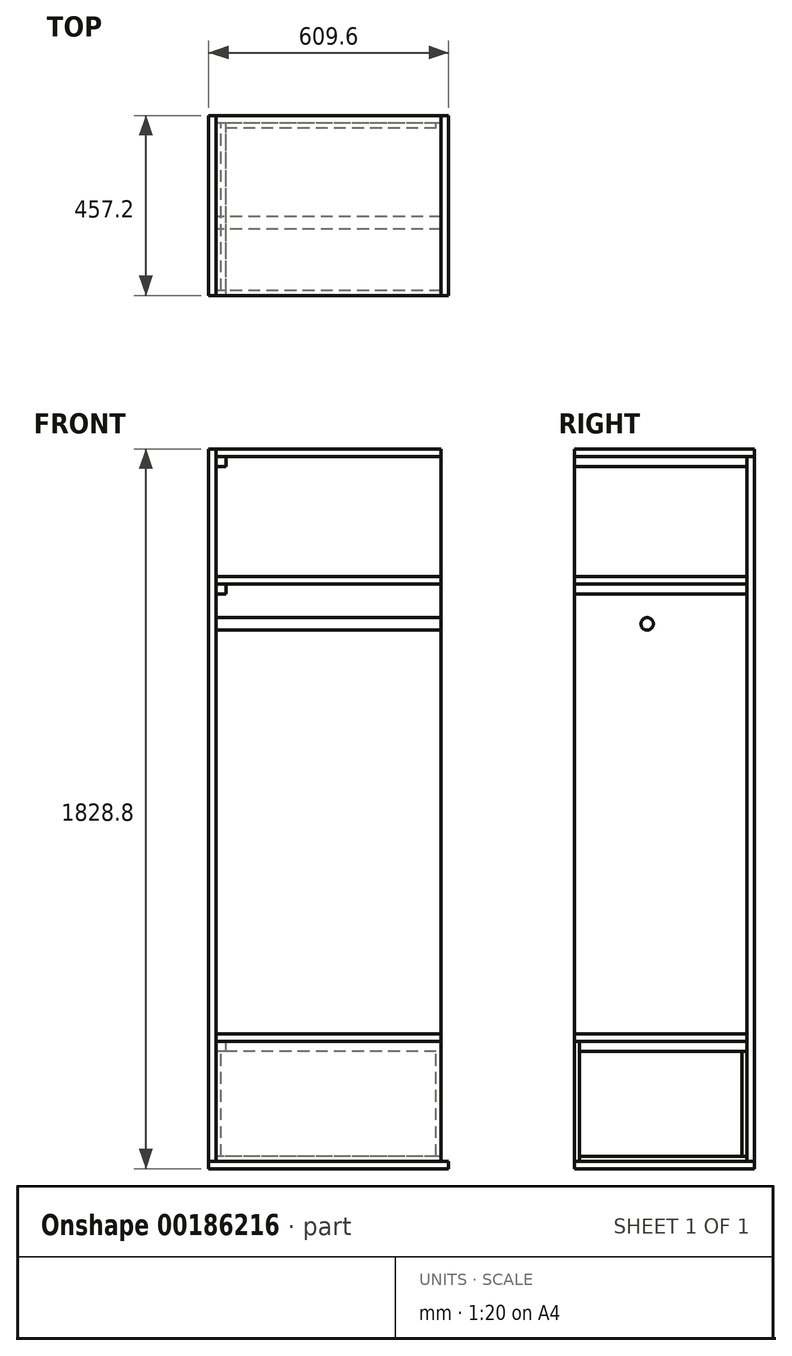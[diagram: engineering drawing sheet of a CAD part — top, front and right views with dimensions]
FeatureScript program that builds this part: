
annotation { "Feature Type Name" : "Feature", "Feature Type Description" : "" }
export const myFeature = defineFeature(function(context is Context, id is Id, definition is map)
    precondition{}
    {
        {
            var Q0;
            Q0=qCreatedBy(makeId("Right.planeOp"),FACE);
            var sketch = newSketch(context, id + "F0", { "sketchPlane" : qUnion([Q0])});
            skLineSegment(sketch, "E0.bottom", {"start": v(-228.6, 914.4) * mm, "end": v(228.6, 914.4) * mm});
            skLineSegment(sketch, "E0.top", {"start": v(-228.6, -914.4) * mm, "end": v(228.6, -914.4) * mm});
            skLineSegment(sketch, "E0.left", {"start": v(-228.6, 914.4) * mm, "end": v(-228.6, -914.4) * mm});
            skLineSegment(sketch, "E0.right", {"start": v(228.6, 914.4) * mm, "end": v(228.6, -914.4) * mm});
            skPoint(sketch, "E0.middle", {"position": v(0, 0) * mm});
            skLineSegment(sketch, "E1", {"start": v(-228.6, 895.35) * mm, "end": v(228.6, 895.35) * mm});
            skLineSegment(sketch, "E2", {"start": v(-228.6, -895.35) * mm, "end": v(228.6, -895.35) * mm});
            skLineSegment(sketch, "E3", {"start": v(-228.6, -571.5) * mm, "end": v(228.6, -571.5) * mm});
            skLineSegment(sketch, "E4", {"start": v(-228.6, -590.55) * mm, "end": v(228.6, -590.55) * mm});
            skLineSegment(sketch, "E5", {"start": v(-228.6, 590.55) * mm, "end": v(228.6, 590.55) * mm});
            skLineSegment(sketch, "E6", {"start": v(-228.6, 571.5) * mm, "end": v(228.6, 571.5) * mm});
            skLineSegment(sketch, "E7", {"start": v(209.55, -914.4) * mm, "end": v(209.55, 914.4) * mm});
            skPoint(sketch, "E8", {"position": v(-44.45, 469.9) * mm});
            skCircle(sketch, "E9", {"center": v(-44.45, 469.9) * mm, "radius": 15.88 * mm});
            skLineSegment(sketch, "E10", {"start": v(-215.9, 914.4) * mm, "end": v(-215.9, -914.4) * mm});
            skLineSegment(sketch, "E11", {"start": v(-228.6, -615.95) * mm, "end": v(209.55, -615.95) * mm});
            skLineSegment(sketch, "E12", {"start": v(209.55, 546.1) * mm, "end": v(-228.6, 546.1) * mm});
            skLineSegment(sketch, "E13", {"start": v(209.55, 869.95) * mm, "end": v(-228.6, 869.95) * mm});
            skLineSegment(sketch, "E14", {"start": v(-215.9, -882.65) * mm, "end": v(209.55, -882.65) * mm});
            skLineSegment(sketch, "E15", {"start": v(196.85, -615.95) * mm, "end": v(196.85, -882.65) * mm});
            skSolve(sketch);
        }
        {
            var Q0;
            {var subQ0=sQuery(id+"F0.wireOp",EDGE,"E0.left");var subQ1=sQuery(id+"F0.wireOp",EDGE,"E0.bottom");var subQ2=makeQuery(id+"F0.imprint","INTERSECT",VERTEX,{"derivedFrom":[subQ1,subQ0]});Q0=makeQuery(id+"F0.imprint","IMPRINT",FACE,{"disambiguationData":[TD([[makeQuery(id+"F0.imprint","IMPRINT",EDGE,{"disambiguationData":[TD([[subQ2,-1.0]])],"derivedFrom":subQ1}),-1.0]])]});}
            var Q1;
            {var subQ0=sQuery(id+"F0.wireOp",EDGE,"E0.right");var subQ1=sQuery(id+"F0.wireOp",EDGE,"E0.bottom");var subQ2=makeQuery(id+"F0.imprint","INTERSECT",VERTEX,{"derivedFrom":[subQ1,subQ0]});Q1=makeQuery(id+"F0.imprint","IMPRINT",FACE,{"disambiguationData":[TD([[makeQuery(id+"F0.imprint","IMPRINT",EDGE,{"disambiguationData":[TD([[subQ2,1.0]])],"derivedFrom":subQ1}),-1.0]])]});}
            var Q2;
            {var subQ0=sQuery(id+"F0.wireOp",EDGE,"E1");var subQ1=sQuery(id+"F0.wireOp",EDGE,"E0.left");var subQ2=makeQuery(id+"F0.imprint","INTERSECT",VERTEX,{"derivedFrom":[subQ1,subQ0]});Q2=makeQuery(id+"F0.imprint","IMPRINT",FACE,{"disambiguationData":[TD([[makeQuery(id+"F0.imprint","IMPRINT",EDGE,{"disambiguationData":[TD([[subQ2,-1.0]])],"derivedFrom":subQ1}),1.0]])]});}
            var Q3;
            {var subQ0=sQuery(id+"F0.wireOp",EDGE,"E1");var subQ1=sQuery(id+"F0.wireOp",EDGE,"E0.right");var subQ2=makeQuery(id+"F0.imprint","INTERSECT",VERTEX,{"derivedFrom":[subQ1,subQ0]});Q3=makeQuery(id+"F0.imprint","IMPRINT",FACE,{"disambiguationData":[TD([[makeQuery(id+"F0.imprint","IMPRINT",EDGE,{"disambiguationData":[TD([[subQ2,-1.0]])],"derivedFrom":subQ1}),-1.0]])]});}
            var Q4;
            {var subQ0=sQuery(id+"F0.wireOp",EDGE,"E5");var subQ1=sQuery(id+"F0.wireOp",EDGE,"E0.left");var subQ2=makeQuery(id+"F0.imprint","INTERSECT",VERTEX,{"derivedFrom":[subQ1,subQ0]});Q4=makeQuery(id+"F0.imprint","IMPRINT",FACE,{"disambiguationData":[TD([[makeQuery(id+"F0.imprint","IMPRINT",EDGE,{"disambiguationData":[TD([[subQ2,-1.0]])],"derivedFrom":subQ1}),1.0]])]});}
            var Q5;
            {var subQ0=sQuery(id+"F0.wireOp",EDGE,"E5");var subQ1=sQuery(id+"F0.wireOp",EDGE,"E0.right");var subQ2=makeQuery(id+"F0.imprint","INTERSECT",VERTEX,{"derivedFrom":[subQ1,subQ0]});Q5=makeQuery(id+"F0.imprint","IMPRINT",FACE,{"disambiguationData":[TD([[makeQuery(id+"F0.imprint","IMPRINT",EDGE,{"disambiguationData":[TD([[subQ2,-1.0]])],"derivedFrom":subQ1}),-1.0]])]});}
            var Q6;
            {var subQ0=sQuery(id+"F0.wireOp",EDGE,"E3");var subQ1=sQuery(id+"F0.wireOp",EDGE,"E0.left");var subQ2=makeQuery(id+"F0.imprint","INTERSECT",VERTEX,{"derivedFrom":[subQ1,subQ0]});Q6=makeQuery(id+"F0.imprint","IMPRINT",FACE,{"disambiguationData":[TD([[makeQuery(id+"F0.imprint","IMPRINT",EDGE,{"disambiguationData":[TD([[subQ2,1.0]])],"derivedFrom":subQ1}),1.0]])]});}
            var Q7;
            {var subQ0=sQuery(id+"F0.wireOp",EDGE,"E3");var subQ1=sQuery(id+"F0.wireOp",EDGE,"E0.right");var subQ2=makeQuery(id+"F0.imprint","INTERSECT",VERTEX,{"derivedFrom":[subQ1,subQ0]});Q7=makeQuery(id+"F0.imprint","IMPRINT",FACE,{"disambiguationData":[TD([[makeQuery(id+"F0.imprint","IMPRINT",EDGE,{"disambiguationData":[TD([[subQ2,1.0]])],"derivedFrom":subQ1}),-1.0]])]});}
            var Q8;
            {var subQ0=sQuery(id+"F0.wireOp",EDGE,"E3");var subQ1=sQuery(id+"F0.wireOp",EDGE,"E0.left");var subQ2=makeQuery(id+"F0.imprint","INTERSECT",VERTEX,{"derivedFrom":[subQ1,subQ0]});Q8=makeQuery(id+"F0.imprint","IMPRINT",FACE,{"disambiguationData":[TD([[makeQuery(id+"F0.imprint","IMPRINT",EDGE,{"disambiguationData":[TD([[subQ2,-1.0]])],"derivedFrom":subQ1}),1.0]])]});}
            var Q9;
            {var subQ0=sQuery(id+"F0.wireOp",EDGE,"E3");var subQ1=sQuery(id+"F0.wireOp",EDGE,"E0.right");var subQ2=makeQuery(id+"F0.imprint","INTERSECT",VERTEX,{"derivedFrom":[subQ1,subQ0]});Q9=makeQuery(id+"F0.imprint","IMPRINT",FACE,{"disambiguationData":[TD([[makeQuery(id+"F0.imprint","IMPRINT",EDGE,{"disambiguationData":[TD([[subQ2,-1.0]])],"derivedFrom":subQ1}),-1.0]])]});}
            var Q10;
            {var subQ0=sQuery(id+"F0.wireOp",EDGE,"E2");var subQ1=sQuery(id+"F0.wireOp",EDGE,"E0.left");var subQ2=makeQuery(id+"F0.imprint","INTERSECT",VERTEX,{"derivedFrom":[subQ1,subQ0]});Q10=makeQuery(id+"F0.imprint","IMPRINT",FACE,{"disambiguationData":[TD([[makeQuery(id+"F0.imprint","IMPRINT",EDGE,{"disambiguationData":[TD([[subQ2,1.0]])],"derivedFrom":subQ1}),1.0]])]});}
            var Q11;
            {var subQ0=sQuery(id+"F0.wireOp",EDGE,"E2");var subQ1=sQuery(id+"F0.wireOp",EDGE,"E0.right");var subQ2=makeQuery(id+"F0.imprint","INTERSECT",VERTEX,{"derivedFrom":[subQ1,subQ0]});Q11=makeQuery(id+"F0.imprint","IMPRINT",FACE,{"disambiguationData":[TD([[makeQuery(id+"F0.imprint","IMPRINT",EDGE,{"disambiguationData":[TD([[subQ2,1.0]])],"derivedFrom":subQ1}),-1.0]])]});}
            var Q12;
            Q12=makeQuery(id+"F0.imprint","IMPRINT",FACE,{"disambiguationData":[TD([[makeQuery(id+"F0.imprint","IMPRINT",EDGE,{"derivedFrom":sQuery(id+"F0.wireOp",EDGE,"E9")}),1.0]])]});
            var Q13;
            {var subQ0=sQuery(id+"F0.wireOp",EDGE,"E10");var subQ1=sQuery(id+"F0.wireOp",EDGE,"E2");var subQ2=makeQuery(id+"F0.imprint","INTERSECT",VERTEX,{"derivedFrom":[subQ1,subQ0]});Q13=makeQuery(id+"F0.imprint","IMPRINT",FACE,{"disambiguationData":[TD([[makeQuery(id+"F0.imprint","IMPRINT",EDGE,{"disambiguationData":[TD([[subQ2,-1.0]])],"derivedFrom":subQ1}),1.0]])]});}
            var Q14;
            Q14=makeQuery(id+"F0.imprint","IMPRINT",FACE,{"disambiguationData":[TD([[makeQuery(id+"F0.imprint","IMPRINT",EDGE,{"derivedFrom":sQuery(id+"F0.wireOp",EDGE,"E9")}),-1.0]])]});
            var Q15;
            {var subQ0=sQuery(id+"F0.wireOp",EDGE,"E10");var subQ1=sQuery(id+"F0.wireOp",EDGE,"E3");var subQ2=makeQuery(id+"F0.imprint","INTERSECT",VERTEX,{"derivedFrom":[subQ1,subQ0]});Q15=makeQuery(id+"F0.imprint","IMPRINT",FACE,{"disambiguationData":[TD([[makeQuery(id+"F0.imprint","IMPRINT",EDGE,{"disambiguationData":[TD([[subQ2,-1.0]])],"derivedFrom":subQ1}),-1.0]])]});}
            var Q16;
            {var subQ0=sQuery(id+"F0.wireOp",EDGE,"E7");var subQ1=sQuery(id+"F0.wireOp",EDGE,"E0.bottom");var subQ2=makeQuery(id+"F0.imprint","INTERSECT",VERTEX,{"derivedFrom":[subQ1,subQ0]});Q16=makeQuery(id+"F0.imprint","IMPRINT",FACE,{"disambiguationData":[TD([[makeQuery(id+"F0.imprint","IMPRINT",EDGE,{"disambiguationData":[TD([[subQ2,1.0]])],"derivedFrom":subQ1}),-1.0]])]});}
            var Q17;
            {var subQ0=sQuery(id+"F0.wireOp",EDGE,"E10");var subQ1=sQuery(id+"F0.wireOp",EDGE,"E1");var subQ2=makeQuery(id+"F0.imprint","INTERSECT",VERTEX,{"derivedFrom":[subQ1,subQ0]});Q17=makeQuery(id+"F0.imprint","IMPRINT",FACE,{"disambiguationData":[TD([[makeQuery(id+"F0.imprint","IMPRINT",EDGE,{"disambiguationData":[TD([[subQ2,-1.0]])],"derivedFrom":subQ1}),-1.0]])]});}
            var Q18;
            {var subQ0=sQuery(id+"F0.wireOp",EDGE,"E10");var subQ1=sQuery(id+"F0.wireOp",EDGE,"E5");var subQ2=makeQuery(id+"F0.imprint","INTERSECT",VERTEX,{"derivedFrom":[subQ1,subQ0]});Q18=makeQuery(id+"F0.imprint","IMPRINT",FACE,{"disambiguationData":[TD([[makeQuery(id+"F0.imprint","IMPRINT",EDGE,{"disambiguationData":[TD([[subQ2,-1.0]])],"derivedFrom":subQ1}),-1.0]])]});}
            var Q19;
            {var subQ5=sQuery(id+"F0.wireOp",EDGE,"E13");Q19=makeQuery(id+"F0.imprint","IMPRINT",FACE,{"disambiguationData":[TD([[makeQuery(id+"F0.imprint","IMPRINT",EDGE,{"derivedFrom":subQ5}),1.0]])]});}
            var Q20;
            {var subQ5=sQuery(id+"F0.wireOp",EDGE,"E12");Q20=makeQuery(id+"F0.imprint","IMPRINT",FACE,{"disambiguationData":[TD([[makeQuery(id+"F0.imprint","IMPRINT",EDGE,{"derivedFrom":subQ5}),-1.0]])]});}
            var Q21;
            {var subQ5=sQuery(id+"F0.wireOp",EDGE,"E11");Q21=makeQuery(id+"F0.imprint","IMPRINT",FACE,{"disambiguationData":[TD([[makeQuery(id+"F0.imprint","IMPRINT",EDGE,{"derivedFrom":subQ5}),1.0]])]});}
            var Q22;
            {var subQ0=sQuery(id+"F0.wireOp",EDGE,"E11");Q22=makeQuery(id+"F0.imprint","IMPRINT",FACE,{"disambiguationData":[TD([[makeQuery(id+"F0.imprint","IMPRINT",EDGE,{"derivedFrom":subQ0}),-1.0]])]});}
            var Q23;
            {var subQ0=sQuery(id+"F0.wireOp",EDGE,"E4");var subQ1=sQuery(id+"F0.wireOp",EDGE,"E0.left");var subQ2=makeQuery(id+"F0.imprint","INTERSECT",VERTEX,{"derivedFrom":[subQ1,subQ0]});Q23=makeQuery(id+"F0.imprint","IMPRINT",FACE,{"disambiguationData":[TD([[makeQuery(id+"F0.imprint","IMPRINT",EDGE,{"disambiguationData":[TD([[subQ2,-1.0]])],"derivedFrom":subQ1}),1.0]])]});}
            extrude(context, id + "F1", {"entities" : qUnion([Q0, Q1, Q2, Q3, Q4, Q5, Q6, Q7, Q8, Q9, Q10, Q11, Q12, Q13, Q14, Q15, Q16, Q17, Q18, Q19, Q20, Q21, Q22, Q23]), "depth" : 19.05 * mm});
        }
        {
            var Q0;
            {var subQ0=sQuery(id+"F0.wireOp",EDGE,"E3");var subQ1=sQuery(id+"F0.wireOp",EDGE,"E0.right");var subQ2=makeQuery(id+"F0.imprint","INTERSECT",VERTEX,{"derivedFrom":[subQ1,subQ0]});Q0=makeQuery(id+"F0.imprint","IMPRINT",FACE,{"disambiguationData":[TD([[makeQuery(id+"F0.imprint","IMPRINT",EDGE,{"disambiguationData":[TD([[subQ2,1.0]])],"derivedFrom":subQ1}),-1.0]])]});}
            var Q1;
            {var subQ0=sQuery(id+"F0.wireOp",EDGE,"E3");var subQ1=sQuery(id+"F0.wireOp",EDGE,"E0.right");var subQ2=makeQuery(id+"F0.imprint","INTERSECT",VERTEX,{"derivedFrom":[subQ1,subQ0]});Q1=makeQuery(id+"F0.imprint","IMPRINT",FACE,{"disambiguationData":[TD([[makeQuery(id+"F0.imprint","IMPRINT",EDGE,{"disambiguationData":[TD([[subQ2,-1.0]])],"derivedFrom":subQ1}),-1.0]])]});}
            var Q2;
            {var subQ0=sQuery(id+"F0.wireOp",EDGE,"E2");var subQ1=sQuery(id+"F0.wireOp",EDGE,"E0.right");var subQ2=makeQuery(id+"F0.imprint","INTERSECT",VERTEX,{"derivedFrom":[subQ1,subQ0]});Q2=makeQuery(id+"F0.imprint","IMPRINT",FACE,{"disambiguationData":[TD([[makeQuery(id+"F0.imprint","IMPRINT",EDGE,{"disambiguationData":[TD([[subQ2,1.0]])],"derivedFrom":subQ1}),-1.0]])]});}
            var Q3;
            {var subQ0=sQuery(id+"F0.wireOp",EDGE,"E5");var subQ1=sQuery(id+"F0.wireOp",EDGE,"E0.right");var subQ2=makeQuery(id+"F0.imprint","INTERSECT",VERTEX,{"derivedFrom":[subQ1,subQ0]});Q3=makeQuery(id+"F0.imprint","IMPRINT",FACE,{"disambiguationData":[TD([[makeQuery(id+"F0.imprint","IMPRINT",EDGE,{"disambiguationData":[TD([[subQ2,-1.0]])],"derivedFrom":subQ1}),-1.0]])]});}
            var Q4;
            {var subQ0=sQuery(id+"F0.wireOp",EDGE,"E1");var subQ1=sQuery(id+"F0.wireOp",EDGE,"E0.right");var subQ2=makeQuery(id+"F0.imprint","INTERSECT",VERTEX,{"derivedFrom":[subQ1,subQ0]});Q4=makeQuery(id+"F0.imprint","IMPRINT",FACE,{"disambiguationData":[TD([[makeQuery(id+"F0.imprint","IMPRINT",EDGE,{"disambiguationData":[TD([[subQ2,-1.0]])],"derivedFrom":subQ1}),-1.0]])]});}
            extrude(context, id + "F2", {"entities" : qUnion([Q0, Q1, Q2, Q3, Q4]), "depth" : 590.55 * mm, "hasSecondDirection" : true, "secondDirectionOppositeDirection" : false, "secondDirectionDepth" : 19.05 * mm});
        }
        {
            var Q0;
            {var subQ0=sQuery(id+"F0.wireOp",EDGE,"E3");var subQ1=sQuery(id+"F0.wireOp",EDGE,"E0.left");var subQ2=makeQuery(id+"F0.imprint","INTERSECT",VERTEX,{"derivedFrom":[subQ1,subQ0]});Q0=makeQuery(id+"F0.imprint","IMPRINT",FACE,{"disambiguationData":[TD([[makeQuery(id+"F0.imprint","IMPRINT",EDGE,{"disambiguationData":[TD([[subQ2,-1.0]])],"derivedFrom":subQ1}),1.0]])]});}
            var Q1;
            {var subQ0=sQuery(id+"F0.wireOp",EDGE,"E5");var subQ1=sQuery(id+"F0.wireOp",EDGE,"E0.left");var subQ2=makeQuery(id+"F0.imprint","INTERSECT",VERTEX,{"derivedFrom":[subQ1,subQ0]});Q1=makeQuery(id+"F0.imprint","IMPRINT",FACE,{"disambiguationData":[TD([[makeQuery(id+"F0.imprint","IMPRINT",EDGE,{"disambiguationData":[TD([[subQ2,-1.0]])],"derivedFrom":subQ1}),1.0]])]});}
            var Q2;
            {var subQ0=sQuery(id+"F0.wireOp",EDGE,"E0.left");var subQ1=sQuery(id+"F0.wireOp",EDGE,"E0.bottom");var subQ2=makeQuery(id+"F0.imprint","INTERSECT",VERTEX,{"derivedFrom":[subQ1,subQ0]});Q2=makeQuery(id+"F0.imprint","IMPRINT",FACE,{"disambiguationData":[TD([[makeQuery(id+"F0.imprint","IMPRINT",EDGE,{"disambiguationData":[TD([[subQ2,-1.0]])],"derivedFrom":subQ1}),-1.0]])]});}
            var Q3;
            {var subQ0=sQuery(id+"F0.wireOp",EDGE,"E0.right");var subQ1=sQuery(id+"F0.wireOp",EDGE,"E0.bottom");var subQ2=makeQuery(id+"F0.imprint","INTERSECT",VERTEX,{"derivedFrom":[subQ1,subQ0]});Q3=makeQuery(id+"F0.imprint","IMPRINT",FACE,{"disambiguationData":[TD([[makeQuery(id+"F0.imprint","IMPRINT",EDGE,{"disambiguationData":[TD([[subQ2,1.0]])],"derivedFrom":subQ1}),-1.0]])]});}
            var Q4;
            {var subQ0=sQuery(id+"F0.wireOp",EDGE,"E7");var subQ1=sQuery(id+"F0.wireOp",EDGE,"E0.bottom");var subQ2=makeQuery(id+"F0.imprint","INTERSECT",VERTEX,{"derivedFrom":[subQ1,subQ0]});Q4=makeQuery(id+"F0.imprint","IMPRINT",FACE,{"disambiguationData":[TD([[makeQuery(id+"F0.imprint","IMPRINT",EDGE,{"disambiguationData":[TD([[subQ2,1.0]])],"derivedFrom":subQ1}),-1.0]])]});}
            var Q5;
            {var subQ0=sQuery(id+"F0.wireOp",EDGE,"E10");var subQ1=sQuery(id+"F0.wireOp",EDGE,"E5");var subQ2=makeQuery(id+"F0.imprint","INTERSECT",VERTEX,{"derivedFrom":[subQ1,subQ0]});Q5=makeQuery(id+"F0.imprint","IMPRINT",FACE,{"disambiguationData":[TD([[makeQuery(id+"F0.imprint","IMPRINT",EDGE,{"disambiguationData":[TD([[subQ2,-1.0]])],"derivedFrom":subQ1}),-1.0]])]});}
            var Q6;
            {var subQ0=sQuery(id+"F0.wireOp",EDGE,"E10");var subQ1=sQuery(id+"F0.wireOp",EDGE,"E3");var subQ2=makeQuery(id+"F0.imprint","INTERSECT",VERTEX,{"derivedFrom":[subQ1,subQ0]});Q6=makeQuery(id+"F0.imprint","IMPRINT",FACE,{"disambiguationData":[TD([[makeQuery(id+"F0.imprint","IMPRINT",EDGE,{"disambiguationData":[TD([[subQ2,-1.0]])],"derivedFrom":subQ1}),-1.0]])]});}
            extrude(context, id + "F3", {"entities" : qUnion([Q0, Q1, Q2, Q3, Q4, Q5, Q6]), "depth" : 590.55 * mm, "hasSecondDirection" : true, "secondDirectionOppositeDirection" : false, "secondDirectionDepth" : 19.05 * mm});
        }
        {
            var Q0;
            {var subQ0=sQuery(id+"F0.wireOp",EDGE,"E0.left");var subQ1=sQuery(id+"F0.wireOp",EDGE,"E0.top");var subQ2=makeQuery(id+"F0.imprint","INTERSECT",VERTEX,{"derivedFrom":[subQ1,subQ0]});Q0=makeQuery(id+"F0.imprint","IMPRINT",FACE,{"disambiguationData":[TD([[makeQuery(id+"F0.imprint","IMPRINT",EDGE,{"disambiguationData":[TD([[subQ2,-1.0]])],"derivedFrom":subQ1}),1.0]])]});}
            var Q1;
            {var subQ0=sQuery(id+"F0.wireOp",EDGE,"E0.right");var subQ1=sQuery(id+"F0.wireOp",EDGE,"E0.top");var subQ2=makeQuery(id+"F0.imprint","INTERSECT",VERTEX,{"derivedFrom":[subQ1,subQ0]});Q1=makeQuery(id+"F0.imprint","IMPRINT",FACE,{"disambiguationData":[TD([[makeQuery(id+"F0.imprint","IMPRINT",EDGE,{"disambiguationData":[TD([[subQ2,1.0]])],"derivedFrom":subQ1}),1.0]])]});}
            var Q2;
            {var subQ0=sQuery(id+"F0.wireOp",EDGE,"E7");var subQ1=sQuery(id+"F0.wireOp",EDGE,"E0.top");var subQ2=makeQuery(id+"F0.imprint","INTERSECT",VERTEX,{"derivedFrom":[subQ1,subQ0]});Q2=makeQuery(id+"F0.imprint","IMPRINT",FACE,{"disambiguationData":[TD([[makeQuery(id+"F0.imprint","IMPRINT",EDGE,{"disambiguationData":[TD([[subQ2,1.0]])],"derivedFrom":subQ1}),1.0]])]});}
            extrude(context, id + "F4", {"entities" : qUnion([Q0, Q1, Q2]), "depth" : 609.6 * mm});
        }
        {
            var Q0;
            Q0=makeQuery(id+"F0.imprint","IMPRINT",FACE,{"disambiguationData":[TD([[makeQuery(id+"F0.imprint","IMPRINT",EDGE,{"derivedFrom":sQuery(id+"F0.wireOp",EDGE,"E9")}),1.0]])]});
            var Q1;
            Q1=sQuery(id+"F0.wireOp",EDGE,"E9");
            extrude(context, id + "F5", {"entities" : qUnion([Q0]), "surfaceEntities" : qUnion([Q1]), "depth" : 590.55 * mm, "hasSecondDirection" : true, "secondDirectionOppositeDirection" : false, "secondDirectionDepth" : 19.05 * mm});
        }
        {
            var Q0;
            {var subQ0=sQuery(id+"F0.wireOp",EDGE,"E10");var subQ1=sQuery(id+"F0.wireOp",EDGE,"E6");var subQ2=makeQuery(id+"F0.imprint","INTERSECT",VERTEX,{"derivedFrom":[subQ1,subQ0]});Q0=makeQuery(id+"F0.imprint","IMPRINT",FACE,{"disambiguationData":[TD([[makeQuery(id+"F0.imprint","IMPRINT",EDGE,{"disambiguationData":[TD([[subQ2,-1.0]])],"derivedFrom":subQ1}),-1.0]])]});}
            var Q1;
            {var subQ2=sQuery(id+"F0.wireOp",EDGE,"E10");var subQ4=sQuery(id+"F0.wireOp",EDGE,"E4");var subQ5=makeQuery(id+"F0.imprint","INTERSECT",VERTEX,{"derivedFrom":[subQ4,subQ2]});Q1=makeQuery(id+"F0.imprint","IMPRINT",FACE,{"disambiguationData":[TD([[makeQuery(id+"F0.imprint","IMPRINT",EDGE,{"disambiguationData":[TD([[subQ5,-1.0]])],"derivedFrom":subQ4}),-1.0]])]});}
            var Q2;
            {var subQ5=sQuery(id+"F0.wireOp",EDGE,"E13");Q2=makeQuery(id+"F0.imprint","IMPRINT",FACE,{"disambiguationData":[TD([[makeQuery(id+"F0.imprint","IMPRINT",EDGE,{"derivedFrom":subQ5}),-1.0]])]});}
            var Q3;
            {var subQ0=sQuery(id+"F0.wireOp",EDGE,"E6");var subQ1=sQuery(id+"F0.wireOp",EDGE,"E0.left");var subQ2=makeQuery(id+"F0.imprint","INTERSECT",VERTEX,{"derivedFrom":[subQ1,subQ0]});Q3=makeQuery(id+"F0.imprint","IMPRINT",FACE,{"disambiguationData":[TD([[makeQuery(id+"F0.imprint","IMPRINT",EDGE,{"disambiguationData":[TD([[subQ2,-1.0]])],"derivedFrom":subQ1}),1.0]])]});}
            extrude(context, id + "F6", {"entities" : qUnion([Q0, Q1, Q2, Q3]), "depth" : 44.45 * mm, "hasSecondDirection" : true, "secondDirectionOppositeDirection" : false, "secondDirectionDepth" : 19.05 * mm});
        }
        {
            var Q0;
            {var subQ4=sQuery(id+"F0.wireOp",EDGE,"E0.left");var subQ6=sQuery(id+"F0.wireOp",EDGE,"E2");var subQ7=makeQuery(id+"F0.imprint","INTERSECT",VERTEX,{"derivedFrom":[subQ4,subQ6]});Q0=makeQuery(id+"F0.imprint","IMPRINT",FACE,{"disambiguationData":[TD([[makeQuery(id+"F0.imprint","IMPRINT",EDGE,{"disambiguationData":[TD([[subQ7,1.0]])],"derivedFrom":subQ4}),1.0]])]});}
            var Q1;
            {var subQ0=sQuery(id+"F0.wireOp",EDGE,"E4");var subQ1=sQuery(id+"F0.wireOp",EDGE,"E0.left");var subQ2=makeQuery(id+"F0.imprint","INTERSECT",VERTEX,{"derivedFrom":[subQ1,subQ0]});Q1=makeQuery(id+"F0.imprint","IMPRINT",FACE,{"disambiguationData":[TD([[makeQuery(id+"F0.imprint","IMPRINT",EDGE,{"disambiguationData":[TD([[subQ2,-1.0]])],"derivedFrom":subQ1}),1.0]])]});}
            extrude(context, id + "F7", {"entities" : qUnion([Q0, Q1]), "depth" : 590.55 * mm, "hasSecondDirection" : true, "secondDirectionOppositeDirection" : false, "secondDirectionDepth" : 19.05 * mm});
        }
        {
            var Q0;
            {var subQ5=sQuery(id+"F0.wireOp",EDGE,"E14");Q0=makeQuery(id+"F0.imprint","IMPRINT",FACE,{"disambiguationData":[TD([[makeQuery(id+"F0.imprint","IMPRINT",EDGE,{"derivedFrom":subQ5}),-1.0]])]});}
            extrude(context, id + "F8", {"entities" : qUnion([Q0]), "depth" : 590.55 * mm, "hasSecondDirection" : true, "secondDirectionOppositeDirection" : false, "secondDirectionDepth" : 19.05 * mm});
        }
        {
            var Q0;
            {var subQ0=sQuery(id+"F0.wireOp",EDGE,"E11");Q0=makeQuery(id+"F0.imprint","IMPRINT",FACE,{"disambiguationData":[TD([[makeQuery(id+"F0.imprint","IMPRINT",EDGE,{"derivedFrom":subQ0}),-1.0]])]});}
            extrude(context, id + "F9", {"entities" : qUnion([Q0]), "depth" : 31.75 * mm, "hasSecondDirection" : true, "secondDirectionOppositeDirection" : false, "secondDirectionDepth" : 19.05 * mm});
        }
        {
            var Q0;
            {var subQ5=sQuery(id+"F0.wireOp",EDGE,"E15");Q0=makeQuery(id+"F0.imprint","IMPRINT",FACE,{"disambiguationData":[TD([[makeQuery(id+"F0.imprint","IMPRINT",EDGE,{"derivedFrom":subQ5}),1.0]])]});}
            extrude(context, id + "F10", {"entities" : qUnion([Q0]), "depth" : 577.85 * mm, "hasSecondDirection" : true, "secondDirectionOppositeDirection" : false, "secondDirectionDepth" : 31.75 * mm});
        }
    });
